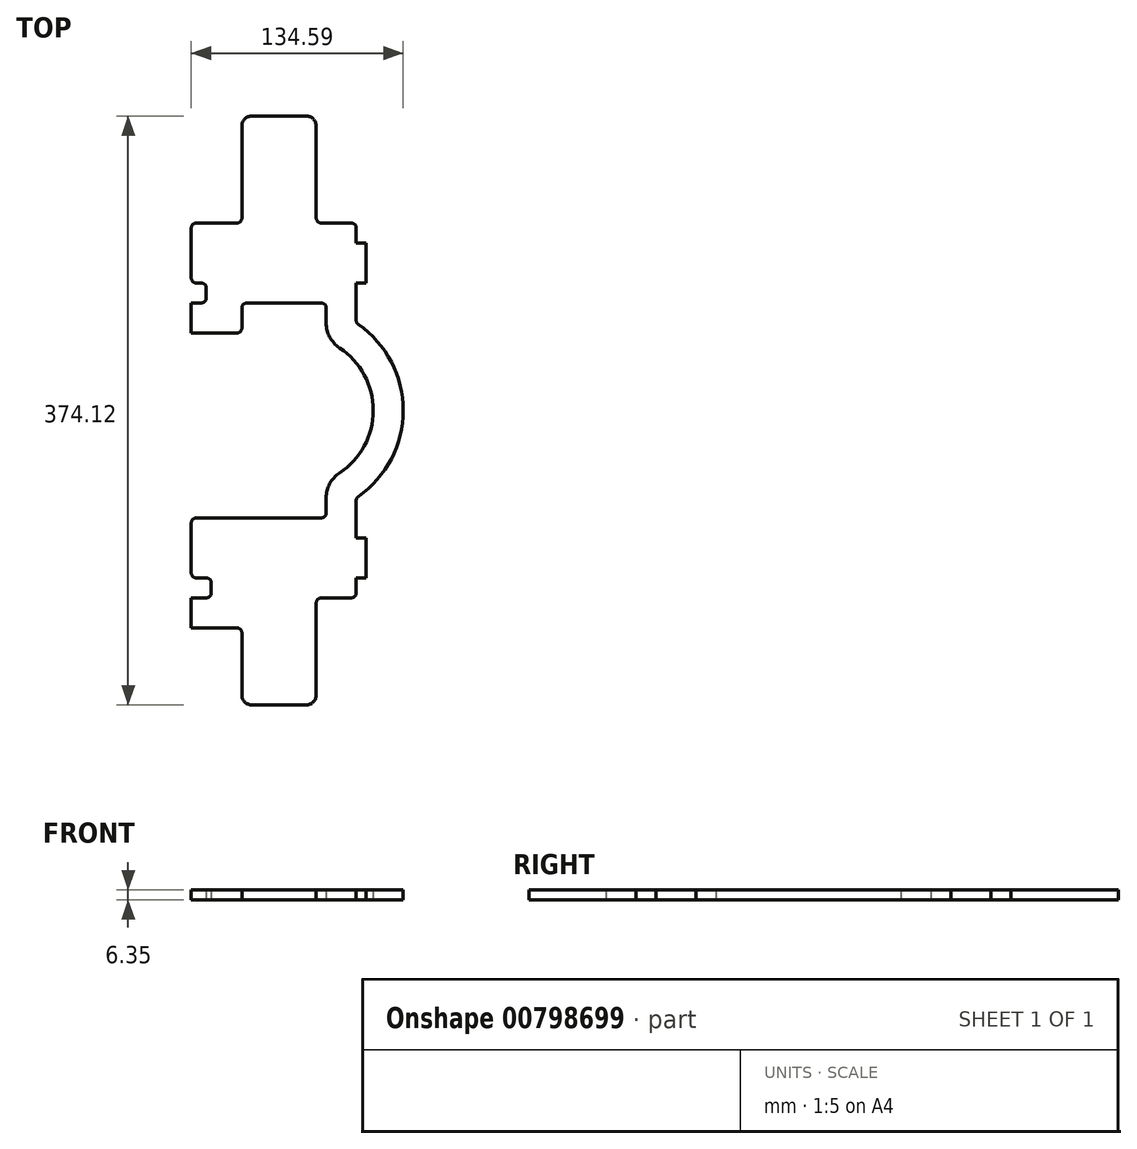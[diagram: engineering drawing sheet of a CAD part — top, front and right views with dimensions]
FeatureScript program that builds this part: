
annotation { "Feature Type Name" : "Feature", "Feature Type Description" : "" }
export const myFeature = defineFeature(function(context is Context, id is Id, definition is map)
    precondition{}
    {
        {
            var Q0;
            Q0=qCreatedBy(makeId("Top.planeOp"),FACE);
            var sketch = newSketch(context, id + "F0", { "sketchPlane" : qUnion([Q0])});
            skLineSegment(sketch, "E0.bottom", {"start": v(0, 0) * mm, "end": v(6.35, 0) * mm});
            skLineSegment(sketch, "E0.top", {"start": v(3.17, 50.8) * mm, "end": v(28.96, 50.8) * mm});
            skLineSegment(sketch, "E0.left", {"start": v(0, 15.88) * mm, "end": v(0, 47.63) * mm});
            skLineSegment(sketch, "E0.right", {"start": v(111.12, 12.7) * mm, "end": v(111.12, 38.1) * mm});
            skLineSegment(sketch, "E1.top", {"start": v(111.12, 38.1) * mm, "end": v(104.78, 38.1) * mm});
            skLineSegment(sketch, "E1.right", {"start": v(104.78, 50.8) * mm, "end": v(104.78, 38.1) * mm});
            skLineSegment(sketch, "E2.top", {"start": v(111.12, 12.7) * mm, "end": v(104.78, 12.7) * mm});
            skLineSegment(sketch, "E2.right", {"start": v(104.78, -11.02) * mm, "end": v(104.78, 12.7) * mm});
            skLineSegment(sketch, "E3.0", {"start": v(79.38, 112.45) * mm, "end": v(79.38, 53.98) * mm});
            skLineSegment(sketch, "E4.0", {"start": v(38.48, 118.8) * mm, "end": v(73.03, 118.8) * mm});
            skLineSegment(sketch, "E5.0", {"start": v(32.13, 112.45) * mm, "end": v(32.13, 53.98) * mm});
            skLineSegment(sketch, "E6.trimOffspring", {"start": v(82.55, 50.8) * mm, "end": v(104.78, 50.8) * mm});
            skPoint(sketch, "E7.visualSharp", {"position": v(32.13, 118.8) * mm});
            skArc(sketch, "E7.filletArc", {"start": v(38.48, 118.8) * mm, "mid": v(34, 116.94) * mm, "end": v(32.13, 112.45) * mm});
            skPoint(sketch, "E8.visualSharp", {"position": v(79.38, 118.8) * mm});
            skArc(sketch, "E8.filletArc", {"start": v(79.38, 112.45) * mm, "mid": v(77.52, 116.94) * mm, "end": v(73.03, 118.8) * mm});
            skLineSegment(sketch, "E9.0", {"start": v(0, -68.26) * mm, "end": v(104.78, -68.26) * mm, "construction": true});
            skArc(sketch, "E10.MirrorCS", {"start": v(38.48, -255.32) * mm, "mid": v(34, -253.46) * mm, "end": v(32.13, -248.97) * mm});
            skArc(sketch, "E11.MirrorCS", {"start": v(79.38, -248.97) * mm, "mid": v(77.52, -253.46) * mm, "end": v(73.03, -255.32) * mm});
            skLineSegment(sketch, "E12.MirrorCS", {"start": v(104.78, -187.33) * mm, "end": v(104.78, -174.62) * mm});
            skLineSegment(sketch, "E13.MirrorCS", {"start": v(12.7, -184.15) * mm, "end": v(12.7, -177.8) * mm});
            skLineSegment(sketch, "E14.MirrorCS", {"start": v(111.12, -174.62) * mm, "end": v(104.78, -174.62) * mm});
            skLineSegment(sketch, "E15.MirrorCS", {"start": v(111.12, -149.22) * mm, "end": v(104.78, -149.22) * mm});
            skLineSegment(sketch, "E16.MirrorCS", {"start": v(104.78, -125.5) * mm, "end": v(104.78, -149.22) * mm});
            skLineSegment(sketch, "E17.MirrorCS", {"start": v(0, -187.33) * mm, "end": v(9.52, -187.33) * mm});
            skLineSegment(sketch, "E18.MirrorCS", {"start": v(111.12, -149.23) * mm, "end": v(111.12, -174.63) * mm});
            skLineSegment(sketch, "E19.MirrorCS", {"start": v(3.18, -174.62) * mm, "end": v(9.52, -174.62) * mm});
            skLineSegment(sketch, "E20.MirrorCS", {"start": v(38.48, -255.32) * mm, "end": v(73.03, -255.32) * mm});
            skLineSegment(sketch, "E21.MirrorCS", {"start": v(79.38, -248.97) * mm, "end": v(79.38, -190.5) * mm});
            skLineSegment(sketch, "E22.MirrorCS", {"start": v(32.13, -248.97) * mm, "end": v(32.13, -209.55) * mm});
            skLineSegment(sketch, "E23.MirrorCS", {"start": v(82.55, -187.33) * mm, "end": v(104.78, -187.33) * mm});
            skPoint(sketch, "E24.MirrorP", {"position": v(79.38, -255.32) * mm});
            skLineSegment(sketch, "E25.MirrorCS", {"start": v(3.17, -136.53) * mm, "end": v(82.55, -136.53) * mm});
            skPoint(sketch, "E26.MirrorP", {"position": v(32.13, -255.32) * mm});
            skLineSegment(sketch, "E27.MirrorCS", {"start": v(0, -139.7) * mm, "end": v(0, -171.45) * mm});
            skLineSegment(sketch, "E28.MirrorCS", {"start": v(0, -206.38) * mm, "end": v(28.96, -206.38) * mm});
            skLineSegment(sketch, "E29.0", {"start": v(0, -12.7) * mm, "end": v(104.78, -12.7) * mm, "construction": true});
            skLineSegment(sketch, "E30.0", {"start": v(0, -123.83) * mm, "end": v(104.78, -123.83) * mm, "construction": true});
            skArc(sketch, "E31", {"start": v(106.13, -122.9) * mm, "mid": v(134.6, -68.26) * mm, "end": v(106.13, -13.62) * mm});
            skArc(sketch, "E32.0", {"start": v(94.24, -107.95) * mm, "mid": v(115.54, -68.26) * mm, "end": v(94.24, -28.57) * mm});
            skLineSegment(sketch, "E33.0", {"start": v(85.73, -12.7) * mm, "end": v(85.73, -3.18) * mm});
            skLineSegment(sketch, "E34.0", {"start": v(85.73, -123.82) * mm, "end": v(85.73, -133.35) * mm});
            skPoint(sketch, "E35.orphan", {"position": v(104.78, 0) * mm});
            skPoint(sketch, "E36.orphan", {"position": v(104.78, -136.53) * mm});
            skPoint(sketch, "E37.visualSharp", {"position": v(85.73, -24.1) * mm});
            skArc(sketch, "E37.filletArc", {"start": v(85.73, -12.7) * mm, "mid": v(87.99, -21.7) * mm, "end": v(94.24, -28.57) * mm});
            skPoint(sketch, "E38.visualSharp", {"position": v(85.73, -112.43) * mm});
            skArc(sketch, "E38.filletArc", {"start": v(94.24, -107.95) * mm, "mid": v(87.99, -114.82) * mm, "end": v(85.73, -123.82) * mm});
            skLineSegment(sketch, "E39.top", {"start": v(3.18, 12.7) * mm, "end": v(6.35, 12.7) * mm});
            skLineSegment(sketch, "E39.left", {"start": v(0, -19.05) * mm, "end": v(0, 0) * mm});
            skLineSegment(sketch, "E39.right", {"start": v(9.52, 3.18) * mm, "end": v(9.52, 9.53) * mm});
            skLineSegment(sketch, "E40.0", {"start": v(0, -19.05) * mm, "end": v(28.96, -19.05) * mm});
            skPoint(sketch, "E41.right.end.orphan", {"position": v(12.7, 38.1) * mm});
            skLineSegment(sketch, "E42.trimOffspring", {"start": v(32.13, -3.17) * mm, "end": v(32.13, -15.88) * mm});
            skLineSegment(sketch, "E43.trimOffspring", {"start": v(35.3, 0) * mm, "end": v(82.55, 0) * mm});
            skPoint(sketch, "E44.orphan", {"position": v(0, 0) * mm});
            skLineSegment(sketch, "E45.trimOffspring", {"start": v(0, -187.33) * mm, "end": v(0, -206.38) * mm});
            skPoint(sketch, "E46.visualSharp", {"position": v(79.38, -187.32) * mm});
            skArc(sketch, "E46.filletArc", {"start": v(82.55, -187.33) * mm, "mid": v(80.3, -188.25) * mm, "end": v(79.38, -190.5) * mm});
            skPoint(sketch, "E47.visualSharp", {"position": v(32.13, -206.38) * mm});
            skArc(sketch, "E47.filletArc", {"start": v(32.13, -209.55) * mm, "mid": v(31.2, -207.3) * mm, "end": v(28.96, -206.38) * mm});
            skPoint(sketch, "E48.visualSharp", {"position": v(12.7, -187.33) * mm});
            skArc(sketch, "E48.filletArc", {"start": v(9.52, -187.33) * mm, "mid": v(11.77, -186.4) * mm, "end": v(12.7, -184.15) * mm});
            skPoint(sketch, "E49.visualSharp", {"position": v(12.7, -174.62) * mm});
            skArc(sketch, "E49.filletArc", {"start": v(12.7, -177.8) * mm, "mid": v(11.77, -175.55) * mm, "end": v(9.52, -174.63) * mm});
            skPoint(sketch, "E50.visualSharp", {"position": v(85.73, -136.53) * mm});
            skArc(sketch, "E50.filletArc", {"start": v(82.55, -136.53) * mm, "mid": v(84.8, -135.6) * mm, "end": v(85.73, -133.35) * mm});
            skPoint(sketch, "E51.visualSharp", {"position": v(0, -136.53) * mm});
            skArc(sketch, "E51.filletArc", {"start": v(3.17, -136.53) * mm, "mid": v(0.93, -137.45) * mm, "end": v(0, -139.7) * mm});
            skPoint(sketch, "E52.visualSharp", {"position": v(0, -174.62) * mm});
            skArc(sketch, "E52.filletArc", {"start": v(0, -171.45) * mm, "mid": v(0.93, -173.7) * mm, "end": v(3.17, -174.62) * mm});
            skPoint(sketch, "E53.visualSharp", {"position": v(32.13, 0) * mm});
            skArc(sketch, "E53.filletArc", {"start": v(35.3, 0) * mm, "mid": v(33.06, -0.93) * mm, "end": v(32.13, -3.17) * mm});
            skPoint(sketch, "E54.visualSharp", {"position": v(85.73, 0) * mm});
            skArc(sketch, "E54.filletArc", {"start": v(85.73, -3.18) * mm, "mid": v(84.8, -0.93) * mm, "end": v(82.55, 0) * mm});
            skPoint(sketch, "E55.visualSharp", {"position": v(32.13, -19.05) * mm});
            skArc(sketch, "E55.filletArc", {"start": v(28.96, -19.05) * mm, "mid": v(31.2, -18.12) * mm, "end": v(32.13, -15.88) * mm});
            skPoint(sketch, "E56.visualSharp", {"position": v(32.13, 50.8) * mm});
            skArc(sketch, "E56.filletArc", {"start": v(28.96, 50.8) * mm, "mid": v(31.2, 51.73) * mm, "end": v(32.13, 53.98) * mm});
            skPoint(sketch, "E57.visualSharp", {"position": v(79.38, 50.8) * mm});
            skArc(sketch, "E57.filletArc", {"start": v(79.38, 53.98) * mm, "mid": v(80.3, 51.73) * mm, "end": v(82.55, 50.8) * mm});
            skPoint(sketch, "E58.visualSharp", {"position": v(0, 50.8) * mm});
            skArc(sketch, "E58.filletArc", {"start": v(3.17, 50.8) * mm, "mid": v(0.93, 49.87) * mm, "end": v(0, 47.63) * mm});
            skPoint(sketch, "E59.visualSharp", {"position": v(0, 12.7) * mm});
            skArc(sketch, "E59.filletArc", {"start": v(0, 15.88) * mm, "mid": v(0.93, 13.63) * mm, "end": v(3.18, 12.7) * mm});
            skPoint(sketch, "E60.visualSharp", {"position": v(9.53, 0) * mm});
            skArc(sketch, "E60.filletArc", {"start": v(6.35, 0) * mm, "mid": v(8.6, 0.93) * mm, "end": v(9.52, 3.18) * mm});
            skPoint(sketch, "E61.visualSharp", {"position": v(9.52, 12.7) * mm});
            skArc(sketch, "E61.filletArc", {"start": v(9.52, 9.53) * mm, "mid": v(8.6, 11.77) * mm, "end": v(6.35, 12.7) * mm});
            skPoint(sketch, "E62.visualSharp", {"position": v(104.78, -123.83) * mm});
            skArc(sketch, "E62.filletArc", {"start": v(106.13, -122.9) * mm, "mid": v(105.13, -124.04) * mm, "end": v(104.78, -125.5) * mm});
            skArc(sketch, "E63.filletArc", {"start": v(104.78, -11.02) * mm, "mid": v(105.13, -12.49) * mm, "end": v(106.13, -13.62) * mm});
            skSolve(sketch);
        }
        {
            var Q0;
            {var subQ1=sQuery(id+"F0.wireOp",EDGE,"E0.bottom");Q0=makeQuery(id+"F0.imprint","IMPRINT",FACE,{"disambiguationData":[TD([[makeQuery(id+"F0.imprint","IMPRINT",EDGE,{"derivedFrom":subQ1}),1.0]])]});}
            var Q1;
            Q1=makeQuery(id+"F0.imprint","IMPRINT",FACE,{"disambiguationData":[TD([[makeQuery(id+"F0.imprint","IMPRINT",EDGE,{"derivedFrom":sQuery(id+"F0.wireOp",EDGE,"E0.bottom")}),-1.0]])]});
            extrude(context, id + "F1", {"entities" : qUnion([Q0, Q1]), "depth" : 6.35 * mm, "offsetDistance" : 25.4 * mm});
        }
        {
            var Q0;
            Q0=makeQuery(id+"F1.opExtrude","SWEPT_EDGE",EDGE,{"disambiguationData":[OSD([sQuery(id+"F0.wireOp",EDGE,"E12.MirrorCS"),sQuery(id+"F0.wireOp",EDGE,"E23.MirrorCS")])]});
            var Q1;
            Q1=makeQuery(id+"F1.opExtrude","SWEPT_EDGE",EDGE,{"disambiguationData":[OSD([sQuery(id+"F0.wireOp",EDGE,"E1.right"),sQuery(id+"F0.wireOp",EDGE,"E6.trimOffspring")])]});
            fillet(context, id + "F2", {"entities" : qUnion([Q0, Q1]), "radius" : 3.17 * mm, "tangentPropagation" : true, "allowEdgeOverflow" : false});
        }
    });
